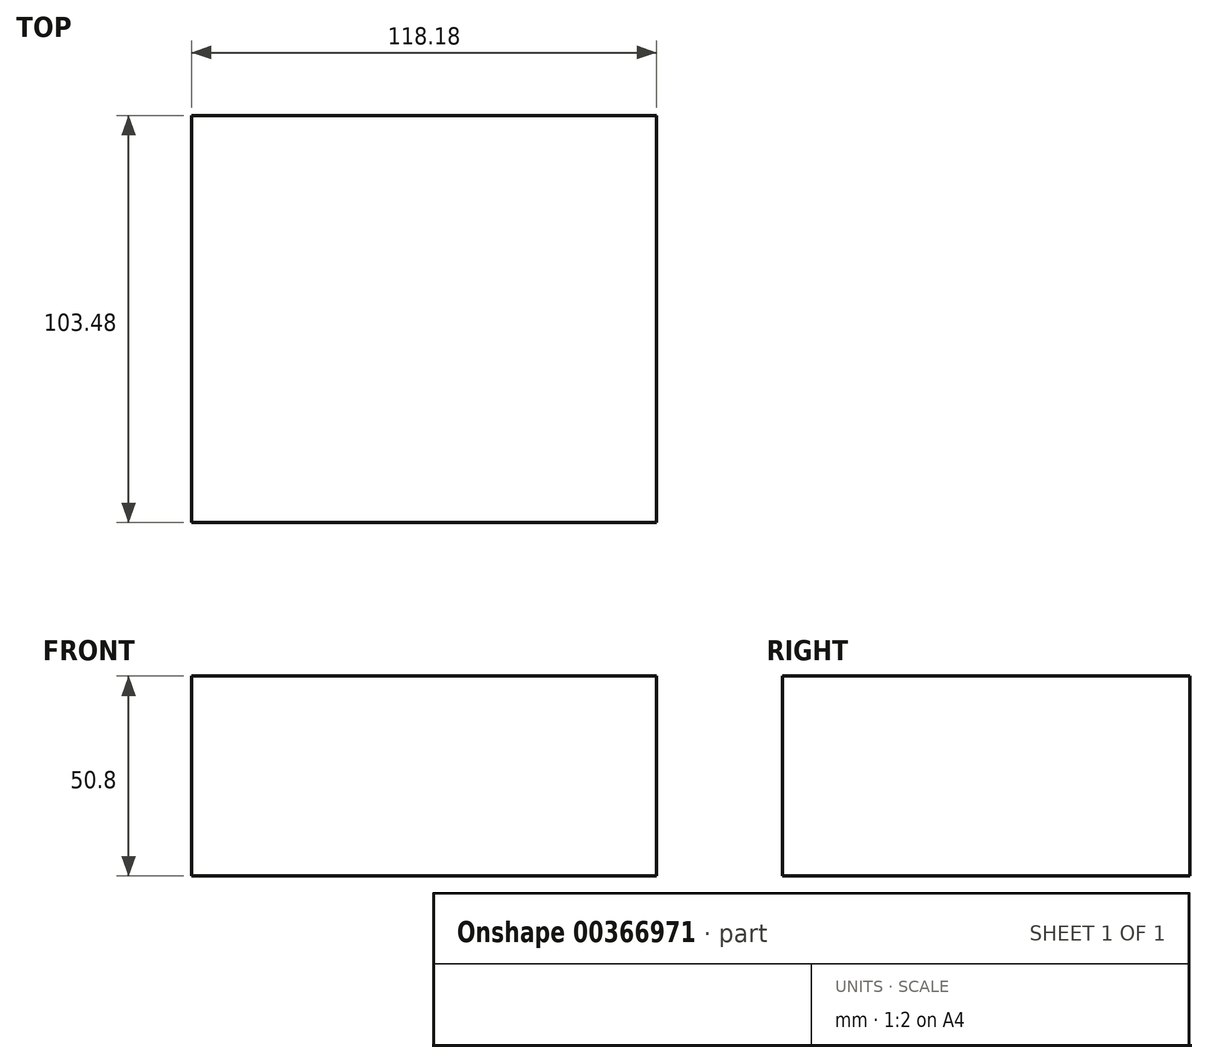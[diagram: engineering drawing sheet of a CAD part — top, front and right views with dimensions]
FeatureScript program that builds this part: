
annotation { "Feature Type Name" : "Feature", "Feature Type Description" : "" }
export const myFeature = defineFeature(function(context is Context, id is Id, definition is map)
    precondition{}
    {
        {
            var Q0;
            Q0=qCreatedBy(makeId("Top.planeOp"),FACE);
            var sketch = newSketch(context, id + "F0", { "sketchPlane" : qUnion([Q0])});
            skLineSegment(sketch, "E0.bottom", {"start": v(59.1, 51.74) * mm, "end": v(-59.1, 51.74) * mm});
            skLineSegment(sketch, "E0.top", {"start": v(59.1, -51.74) * mm, "end": v(-59.1, -51.74) * mm});
            skLineSegment(sketch, "E0.left", {"start": v(59.1, 51.74) * mm, "end": v(59.1, -51.74) * mm});
            skLineSegment(sketch, "E0.right", {"start": v(-59.1, 51.74) * mm, "end": v(-59.1, -51.74) * mm});
            skPoint(sketch, "E0.middle", {"position": v(0, 0) * mm});
            skSolve(sketch);
        }
        {
            var Q0;
            Q0=makeQuery(id+"F0.imprint","IMPRINT",FACE,{"disambiguationData":[TD([[makeQuery(id+"F0.imprint","IMPRINT",EDGE,{"derivedFrom":sQuery(id+"F0.wireOp",EDGE,"E0.bottom")}),1.0]])]});
            extrude(context, id + "F1", {"entities" : qUnion([Q0]), "depth" : 50.8 * mm});
        }
    });
